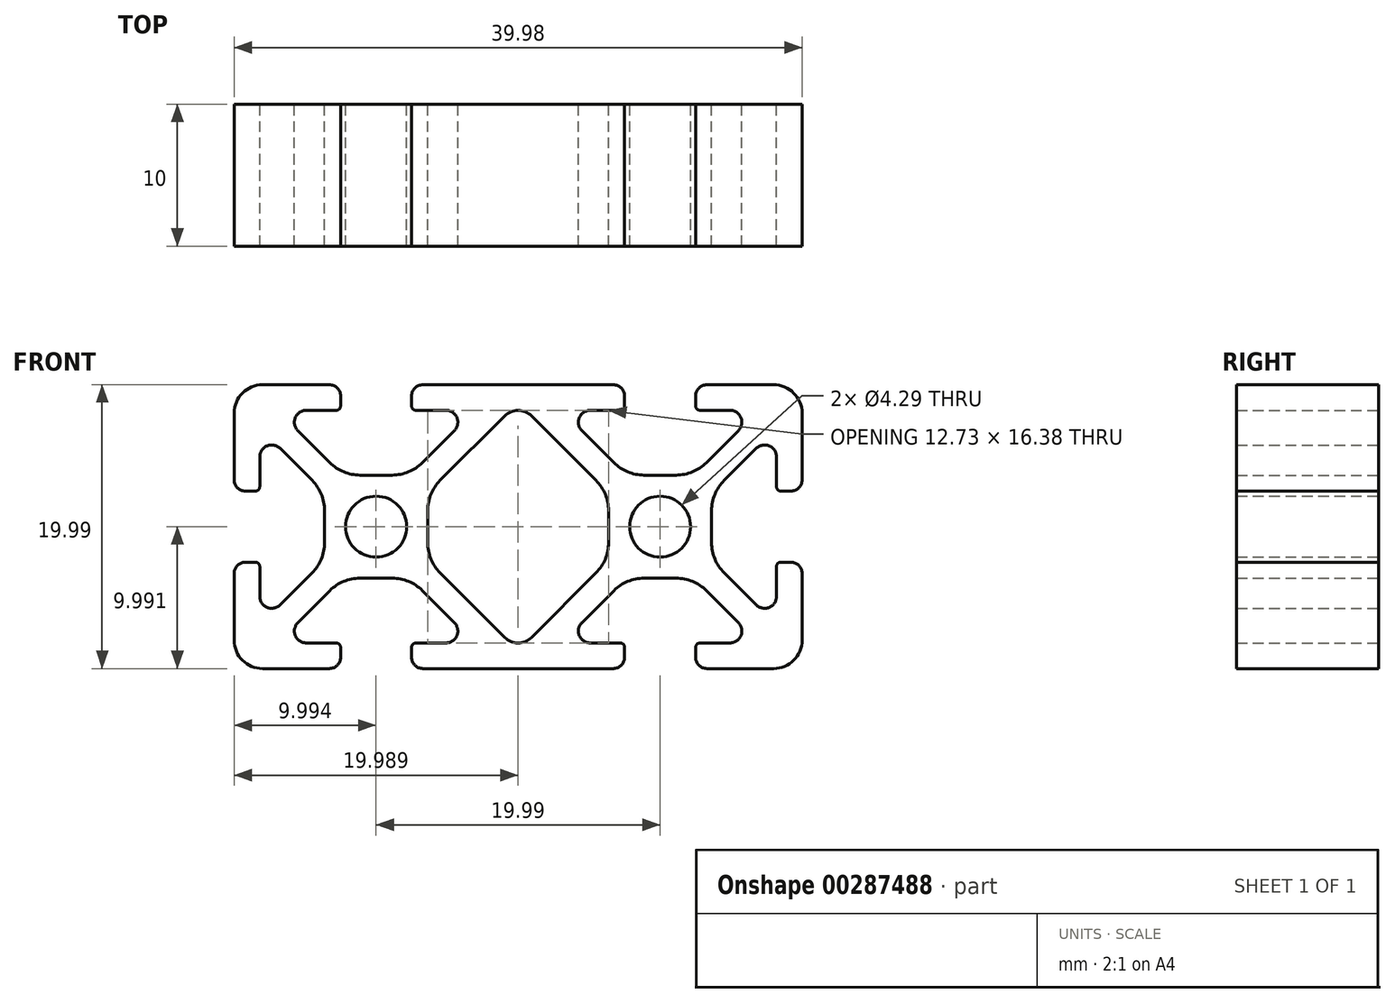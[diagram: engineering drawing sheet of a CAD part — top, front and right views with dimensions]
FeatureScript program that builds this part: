
annotation { "Feature Type Name" : "Feature", "Feature Type Description" : "" }
export const myFeature = defineFeature(function(context is Context, id is Id, definition is map)
    precondition{}
    {
        {
            var Q0;
            Q0=qCreatedBy(makeId("Front.planeOp"),FACE);
            var sketch = newSketch(context, id + "F0", { "sketchPlane" : qUnion([Q0])});
            skArc(sketch, "E0.0.0", {"start": v(-12.02, 4.76) * mm, "mid": v(-13.17, 4.99) * mm, "end": v(-14.14, 5.64) * mm});
            skLineSegment(sketch, "E0.0.1", {"start": v(-14.14, 5.64) * mm, "end": v(-16.4, 7.9) * mm});
            skArc(sketch, "E0.0.2", {"start": v(-16.4, 7.9) * mm, "mid": v(-16.58, 8.8) * mm, "end": v(-15.8, 9.32) * mm});
            skLineSegment(sketch, "E0.0.3", {"start": v(-15.8, 9.32) * mm, "end": v(-13.7, 9.32) * mm});
            skArc(sketch, "E0.0.4", {"start": v(-13.7, 9.32) * mm, "mid": v(-13.48, 9.41) * mm, "end": v(-13.39, 9.63) * mm});
            skLineSegment(sketch, "E0.0.5", {"start": v(-13.39, 9.63) * mm, "end": v(-13.39, 10.34) * mm});
            skArc(sketch, "E0.0.6", {"start": v(-13.39, 10.34) * mm, "mid": v(-13.62, 10.9) * mm, "end": v(-14.18, 11.13) * mm});
            skLineSegment(sketch, "E0.0.7", {"start": v(-14.18, 11.13) * mm, "end": v(-18.87, 11.13) * mm});
            skArc(sketch, "E0.0.8", {"start": v(-18.87, 11.13) * mm, "mid": v(-20.3, 10.54) * mm, "end": v(-20.88, 9.12) * mm});
            skLineSegment(sketch, "E0.0.9", {"start": v(-20.88, 9.12) * mm, "end": v(-20.88, 4.42) * mm});
            skArc(sketch, "E0.0.10", {"start": v(-20.88, 4.42) * mm, "mid": v(-20.65, 3.86) * mm, "end": v(-20.1, 3.63) * mm});
            skLineSegment(sketch, "E0.0.11", {"start": v(-20.1, 3.63) * mm, "end": v(-19.38, 3.63) * mm});
            skArc(sketch, "E0.0.12", {"start": v(-19.38, 3.63) * mm, "mid": v(-19.17, 3.72) * mm, "end": v(-19.08, 3.94) * mm});
            skLineSegment(sketch, "E0.0.13", {"start": v(-19.08, 3.94) * mm, "end": v(-19.08, 6.05) * mm});
            skArc(sketch, "E0.0.14", {"start": v(-19.08, 6.05) * mm, "mid": v(-18.56, 6.82) * mm, "end": v(-17.65, 6.64) * mm});
            skLineSegment(sketch, "E0.0.15", {"start": v(-17.65, 6.64) * mm, "end": v(-15.4, 4.38) * mm});
            skArc(sketch, "E0.0.16", {"start": v(-15.4, 4.38) * mm, "mid": v(-14.74, 3.41) * mm, "end": v(-14.51, 2.26) * mm});
            skLineSegment(sketch, "E0.0.17", {"start": v(-14.51, 2.26) * mm, "end": v(-14.51, 0) * mm});
            skArc(sketch, "E0.0.18", {"start": v(-14.51, 0) * mm, "mid": v(-14.74, -1.15) * mm, "end": v(-15.4, -2.12) * mm});
            skLineSegment(sketch, "E0.0.19", {"start": v(-15.4, -2.12) * mm, "end": v(-17.65, -4.38) * mm});
            skArc(sketch, "E0.0.20", {"start": v(-17.65, -4.38) * mm, "mid": v(-18.56, -4.56) * mm, "end": v(-19.08, -3.78) * mm});
            skLineSegment(sketch, "E0.0.21", {"start": v(-19.08, -3.78) * mm, "end": v(-19.08, -1.68) * mm});
            skArc(sketch, "E0.0.22", {"start": v(-19.08, -1.68) * mm, "mid": v(-19.17, -1.46) * mm, "end": v(-19.38, -1.37) * mm});
            skLineSegment(sketch, "E0.0.23", {"start": v(-19.38, -1.37) * mm, "end": v(-20.1, -1.37) * mm});
            skArc(sketch, "E0.0.24", {"start": v(-20.1, -1.37) * mm, "mid": v(-20.65, -1.6) * mm, "end": v(-20.88, -2.16) * mm});
            skLineSegment(sketch, "E0.0.25", {"start": v(-20.88, -2.16) * mm, "end": v(-20.88, -6.86) * mm});
            skArc(sketch, "E0.0.26", {"start": v(-20.88, -6.86) * mm, "mid": v(-20.3, -8.28) * mm, "end": v(-18.87, -8.86) * mm});
            skLineSegment(sketch, "E0.0.27", {"start": v(-18.87, -8.86) * mm, "end": v(-14.18, -8.86) * mm});
            skArc(sketch, "E0.0.28", {"start": v(-14.18, -8.86) * mm, "mid": v(-13.62, -8.63) * mm, "end": v(-13.39, -8.08) * mm});
            skLineSegment(sketch, "E0.0.29", {"start": v(-13.39, -8.08) * mm, "end": v(-13.39, -7.36) * mm});
            skArc(sketch, "E0.0.30", {"start": v(-13.39, -7.36) * mm, "mid": v(-13.48, -7.15) * mm, "end": v(-13.7, -7.06) * mm});
            skLineSegment(sketch, "E0.0.31", {"start": v(-13.7, -7.06) * mm, "end": v(-15.8, -7.06) * mm});
            skArc(sketch, "E0.0.32", {"start": v(-15.8, -7.06) * mm, "mid": v(-16.58, -6.54) * mm, "end": v(-16.4, -5.63) * mm});
            skLineSegment(sketch, "E0.0.33", {"start": v(-16.4, -5.63) * mm, "end": v(-14.14, -3.37) * mm});
            skArc(sketch, "E0.0.34", {"start": v(-14.14, -3.37) * mm, "mid": v(-13.17, -2.72) * mm, "end": v(-12.02, -2.5) * mm});
            skLineSegment(sketch, "E0.0.35", {"start": v(-12.02, -2.5) * mm, "end": v(-9.75, -2.5) * mm});
            skArc(sketch, "E0.0.36", {"start": v(-9.75, -2.5) * mm, "mid": v(-8.6, -2.72) * mm, "end": v(-7.63, -3.37) * mm});
            skLineSegment(sketch, "E0.0.37", {"start": v(-7.63, -3.37) * mm, "end": v(-5.38, -5.63) * mm});
            skArc(sketch, "E0.0.38", {"start": v(-5.38, -5.63) * mm, "mid": v(-5.2, -6.54) * mm, "end": v(-5.97, -7.06) * mm});
            skLineSegment(sketch, "E0.0.39", {"start": v(-5.97, -7.06) * mm, "end": v(-8.08, -7.06) * mm});
            skArc(sketch, "E0.0.40", {"start": v(-8.08, -7.06) * mm, "mid": v(-8.3, -7.15) * mm, "end": v(-8.38, -7.36) * mm});
            skLineSegment(sketch, "E0.0.41", {"start": v(-8.38, -7.36) * mm, "end": v(-8.38, -8.08) * mm});
            skArc(sketch, "E0.0.42", {"start": v(-8.38, -8.08) * mm, "mid": v(-8.15, -8.63) * mm, "end": v(-7.6, -8.86) * mm});
            skLineSegment(sketch, "E0.0.43", {"start": v(-7.6, -8.86) * mm, "end": v(5.81, -8.86) * mm});
            skArc(sketch, "E0.0.44", {"start": v(5.81, -8.86) * mm, "mid": v(6.37, -8.63) * mm, "end": v(6.6, -8.08) * mm});
            skLineSegment(sketch, "E0.0.45", {"start": v(6.6, -8.08) * mm, "end": v(6.6, -7.36) * mm});
            skArc(sketch, "E0.0.46", {"start": v(6.6, -7.36) * mm, "mid": v(6.51, -7.15) * mm, "end": v(6.3, -7.06) * mm});
            skLineSegment(sketch, "E0.0.47", {"start": v(6.3, -7.06) * mm, "end": v(4.19, -7.06) * mm});
            skArc(sketch, "E0.0.48", {"start": v(4.19, -7.06) * mm, "mid": v(3.41, -6.54) * mm, "end": v(3.6, -5.63) * mm});
            skLineSegment(sketch, "E0.0.49", {"start": v(3.6, -5.63) * mm, "end": v(5.85, -3.37) * mm});
            skArc(sketch, "E0.0.50", {"start": v(5.85, -3.37) * mm, "mid": v(6.82, -2.72) * mm, "end": v(7.97, -2.5) * mm});
            skLineSegment(sketch, "E0.0.51", {"start": v(7.97, -2.5) * mm, "end": v(10.24, -2.5) * mm});
            skArc(sketch, "E0.0.52", {"start": v(10.24, -2.5) * mm, "mid": v(11.38, -2.72) * mm, "end": v(12.36, -3.37) * mm});
            skLineSegment(sketch, "E0.0.53", {"start": v(12.36, -3.37) * mm, "end": v(14.61, -5.63) * mm});
            skArc(sketch, "E0.0.54", {"start": v(14.61, -5.63) * mm, "mid": v(14.8, -6.54) * mm, "end": v(14.02, -7.06) * mm});
            skLineSegment(sketch, "E0.0.55", {"start": v(14.02, -7.06) * mm, "end": v(11.91, -7.06) * mm});
            skArc(sketch, "E0.0.56", {"start": v(11.91, -7.06) * mm, "mid": v(11.7, -7.15) * mm, "end": v(11.6, -7.36) * mm});
            skLineSegment(sketch, "E0.0.57", {"start": v(11.6, -7.36) * mm, "end": v(11.6, -8.08) * mm});
            skArc(sketch, "E0.0.58", {"start": v(11.6, -8.08) * mm, "mid": v(11.84, -8.63) * mm, "end": v(12.4, -8.86) * mm});
            skLineSegment(sketch, "E0.0.59", {"start": v(12.4, -8.86) * mm, "end": v(17.1, -8.86) * mm});
            skArc(sketch, "E0.0.60", {"start": v(17.1, -8.86) * mm, "mid": v(18.51, -8.28) * mm, "end": v(19.1, -6.86) * mm});
            skLineSegment(sketch, "E0.0.61", {"start": v(19.1, -6.86) * mm, "end": v(19.1, -2.16) * mm});
            skArc(sketch, "E0.0.62", {"start": v(19.1, -2.16) * mm, "mid": v(18.87, -1.6) * mm, "end": v(18.31, -1.37) * mm});
            skLineSegment(sketch, "E0.0.63", {"start": v(18.31, -1.37) * mm, "end": v(17.6, -1.37) * mm});
            skArc(sketch, "E0.0.64", {"start": v(17.6, -1.37) * mm, "mid": v(17.38, -1.46) * mm, "end": v(17.3, -1.68) * mm});
            skLineSegment(sketch, "E0.0.65", {"start": v(17.3, -1.68) * mm, "end": v(17.3, -3.78) * mm});
            skArc(sketch, "E0.0.66", {"start": v(17.3, -3.78) * mm, "mid": v(16.78, -4.56) * mm, "end": v(15.86, -4.38) * mm});
            skLineSegment(sketch, "E0.0.67", {"start": v(15.86, -4.38) * mm, "end": v(13.6, -2.12) * mm});
            skArc(sketch, "E0.0.68", {"start": v(13.6, -2.12) * mm, "mid": v(12.96, -1.15) * mm, "end": v(12.73, 0) * mm});
            skLineSegment(sketch, "E0.0.69", {"start": v(12.73, 0) * mm, "end": v(12.73, 2.26) * mm});
            skArc(sketch, "E0.0.70", {"start": v(12.73, 2.26) * mm, "mid": v(12.96, 3.41) * mm, "end": v(13.6, 4.38) * mm});
            skLineSegment(sketch, "E0.0.71", {"start": v(13.6, 4.38) * mm, "end": v(15.86, 6.64) * mm});
            skArc(sketch, "E0.0.72", {"start": v(15.86, 6.64) * mm, "mid": v(16.78, 6.82) * mm, "end": v(17.3, 6.05) * mm});
            skLineSegment(sketch, "E0.0.73", {"start": v(17.3, 6.05) * mm, "end": v(17.3, 3.94) * mm});
            skArc(sketch, "E0.0.74", {"start": v(17.3, 3.94) * mm, "mid": v(17.38, 3.72) * mm, "end": v(17.6, 3.63) * mm});
            skLineSegment(sketch, "E0.0.75", {"start": v(17.6, 3.63) * mm, "end": v(18.31, 3.63) * mm});
            skArc(sketch, "E0.0.76", {"start": v(18.31, 3.63) * mm, "mid": v(18.87, 3.86) * mm, "end": v(19.1, 4.42) * mm});
            skLineSegment(sketch, "E0.0.77", {"start": v(19.1, 4.42) * mm, "end": v(19.1, 9.12) * mm});
            skArc(sketch, "E0.0.78", {"start": v(19.1, 9.12) * mm, "mid": v(18.51, 10.54) * mm, "end": v(17.1, 11.13) * mm});
            skLineSegment(sketch, "E0.0.79", {"start": v(17.1, 11.13) * mm, "end": v(12.4, 11.13) * mm});
            skArc(sketch, "E0.0.80", {"start": v(12.4, 11.13) * mm, "mid": v(11.84, 10.9) * mm, "end": v(11.6, 10.34) * mm});
            skLineSegment(sketch, "E0.0.81", {"start": v(11.6, 10.34) * mm, "end": v(11.6, 9.63) * mm});
            skArc(sketch, "E0.0.82", {"start": v(11.6, 9.63) * mm, "mid": v(11.7, 9.41) * mm, "end": v(11.91, 9.32) * mm});
            skLineSegment(sketch, "E0.0.83", {"start": v(11.91, 9.32) * mm, "end": v(14.02, 9.32) * mm});
            skArc(sketch, "E0.0.84", {"start": v(14.02, 9.32) * mm, "mid": v(14.8, 8.8) * mm, "end": v(14.61, 7.9) * mm});
            skLineSegment(sketch, "E0.0.85", {"start": v(14.61, 7.9) * mm, "end": v(12.36, 5.64) * mm});
            skArc(sketch, "E0.0.86", {"start": v(12.36, 5.64) * mm, "mid": v(11.38, 4.99) * mm, "end": v(10.24, 4.76) * mm});
            skLineSegment(sketch, "E0.0.87", {"start": v(10.24, 4.76) * mm, "end": v(7.97, 4.76) * mm});
            skArc(sketch, "E0.0.88", {"start": v(7.97, 4.76) * mm, "mid": v(6.82, 4.99) * mm, "end": v(5.85, 5.64) * mm});
            skLineSegment(sketch, "E0.0.89", {"start": v(5.85, 5.64) * mm, "end": v(3.6, 7.9) * mm});
            skArc(sketch, "E0.0.90", {"start": v(3.6, 7.9) * mm, "mid": v(3.41, 8.8) * mm, "end": v(4.19, 9.32) * mm});
            skLineSegment(sketch, "E0.0.91", {"start": v(4.19, 9.32) * mm, "end": v(6.3, 9.32) * mm});
            skArc(sketch, "E0.0.92", {"start": v(6.3, 9.32) * mm, "mid": v(6.51, 9.41) * mm, "end": v(6.6, 9.63) * mm});
            skLineSegment(sketch, "E0.0.93", {"start": v(6.6, 9.63) * mm, "end": v(6.6, 10.34) * mm});
            skArc(sketch, "E0.0.94", {"start": v(6.6, 10.34) * mm, "mid": v(6.37, 10.9) * mm, "end": v(5.81, 11.13) * mm});
            skLineSegment(sketch, "E0.0.95", {"start": v(5.81, 11.13) * mm, "end": v(-7.6, 11.13) * mm});
            skArc(sketch, "E0.0.96", {"start": v(-7.6, 11.13) * mm, "mid": v(-8.15, 10.9) * mm, "end": v(-8.38, 10.34) * mm});
            skLineSegment(sketch, "E0.0.97", {"start": v(-8.38, 10.34) * mm, "end": v(-8.38, 9.63) * mm});
            skArc(sketch, "E0.0.98", {"start": v(-8.38, 9.63) * mm, "mid": v(-8.3, 9.41) * mm, "end": v(-8.08, 9.32) * mm});
            skLineSegment(sketch, "E0.0.99", {"start": v(-8.08, 9.32) * mm, "end": v(-5.97, 9.32) * mm});
            skArc(sketch, "E0.0.100", {"start": v(-5.97, 9.32) * mm, "mid": v(-5.2, 8.8) * mm, "end": v(-5.38, 7.9) * mm});
            skLineSegment(sketch, "E0.0.101", {"start": v(-5.38, 7.9) * mm, "end": v(-7.63, 5.64) * mm});
            skArc(sketch, "E0.0.102", {"start": v(-7.63, 5.64) * mm, "mid": v(-8.6, 4.99) * mm, "end": v(-9.75, 4.76) * mm});
            skLineSegment(sketch, "E0.0.103", {"start": v(-9.75, 4.76) * mm, "end": v(-12.02, 4.76) * mm});
            skCircle(sketch, "E1.0", {"center": v(-10.89, 1.13) * mm, "radius": 2.15 * mm});
            skCircle(sketch, "E2.0", {"center": v(9.1, 1.13) * mm, "radius": 2.15 * mm});
            skLineSegment(sketch, "E3.0", {"start": v(-7.26, 2.26) * mm, "end": v(-7.26, 0) * mm});
            skArc(sketch, "E3.1", {"start": v(-6.38, 4.38) * mm, "mid": v(-7.03, 3.41) * mm, "end": v(-7.26, 2.26) * mm});
            skLineSegment(sketch, "E3.2", {"start": v(-1.83, 8.93) * mm, "end": v(-6.38, 4.38) * mm});
            skArc(sketch, "E3.3", {"start": v(-7.26, 0) * mm, "mid": v(-7.03, -1.15) * mm, "end": v(-6.38, -2.12) * mm});
            skLineSegment(sketch, "E3.4", {"start": v(-6.38, -2.12) * mm, "end": v(-1.83, -6.67) * mm});
            skArc(sketch, "E3.5", {"start": v(-1.83, -6.67) * mm, "mid": v(-0.9, -7.06) * mm, "end": v(0.05, -6.67) * mm});
            skLineSegment(sketch, "E3.6", {"start": v(0.05, -6.67) * mm, "end": v(4.6, -2.12) * mm});
            skLineSegment(sketch, "E3.7", {"start": v(4.6, 4.38) * mm, "end": v(0.05, 8.93) * mm});
            skLineSegment(sketch, "E3.8", {"start": v(5.48, 0) * mm, "end": v(5.48, 2.26) * mm});
            skArc(sketch, "E3.9", {"start": v(5.48, 2.26) * mm, "mid": v(5.25, 3.41) * mm, "end": v(4.6, 4.38) * mm});
            skArc(sketch, "E3.10", {"start": v(4.6, -2.12) * mm, "mid": v(5.25, -1.15) * mm, "end": v(5.48, 0) * mm});
            skArc(sketch, "E3.11", {"start": v(0.05, 8.93) * mm, "mid": v(-0.9, 9.32) * mm, "end": v(-1.83, 8.93) * mm});
            skSolve(sketch);
        }
        {
            var Q0;
            Q0 = qSketchRegion(id + "F0", true);
            extrude(context, id + "F1", {"entities" : qUnion([Q0]), "depth" : 10 * mm});
        }
    });
